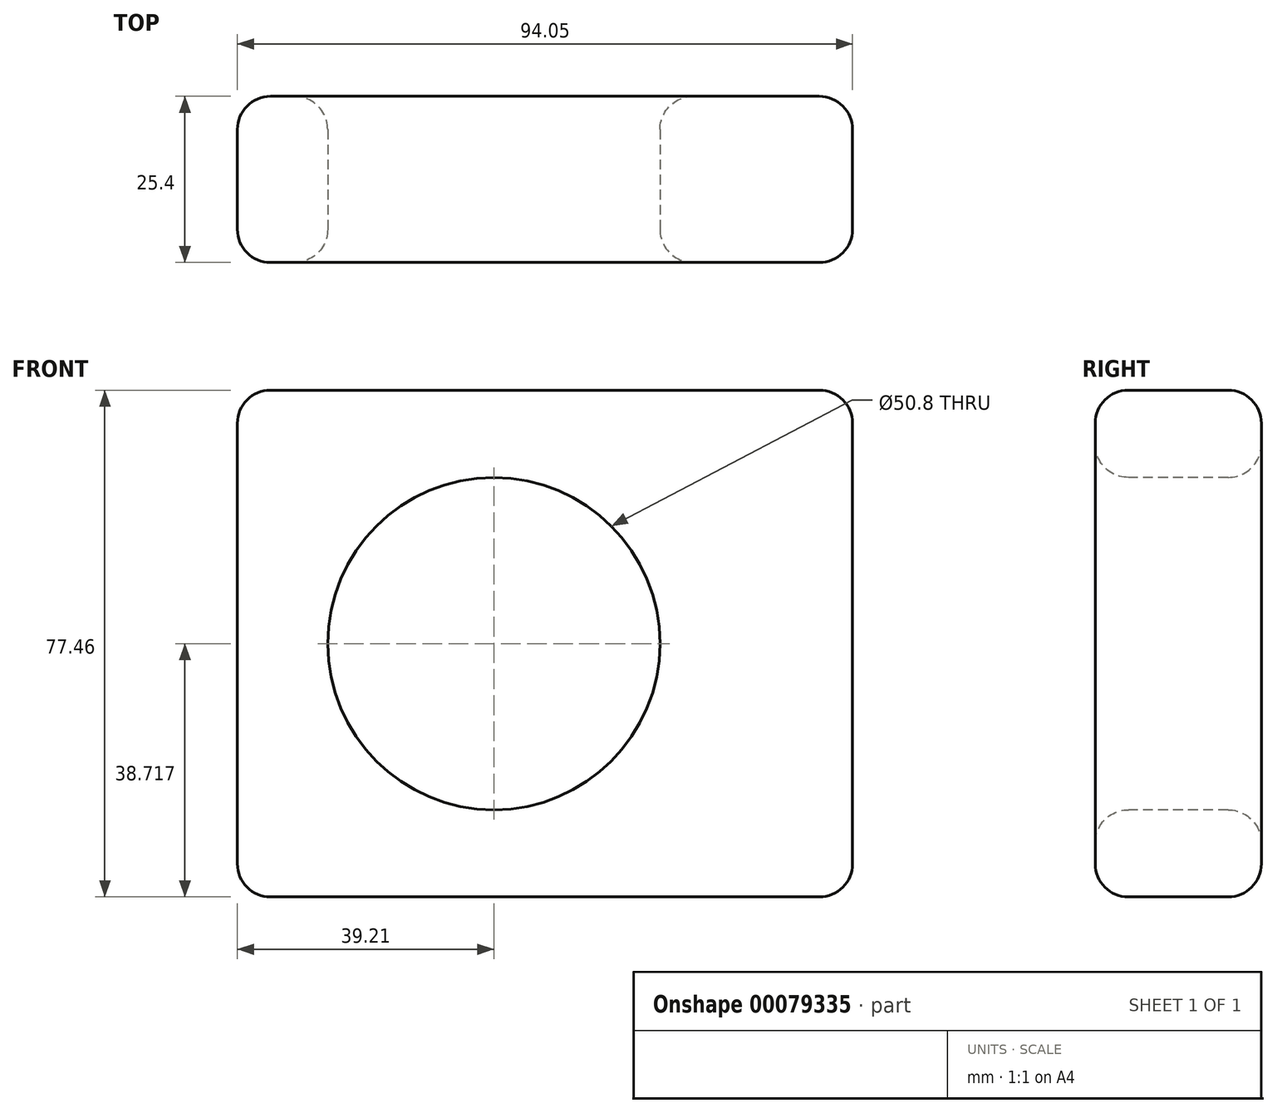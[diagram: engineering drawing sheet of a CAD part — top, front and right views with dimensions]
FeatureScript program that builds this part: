
annotation { "Feature Type Name" : "Feature", "Feature Type Description" : "" }
export const myFeature = defineFeature(function(context is Context, id is Id, definition is map)
    precondition{}
    {
        {
            var Q0;
            Q0=qCreatedBy(makeId("Front.planeOp"),FACE);
            var sketch = newSketch(context, id + "F0", { "sketchPlane" : qUnion([Q0])});
            skLineSegment(sketch, "E0.bottom", {"start": v(24.22, -20.71) * mm, "end": v(-69.83, -20.71) * mm});
            skLineSegment(sketch, "E0.top", {"start": v(24.22, 56.75) * mm, "end": v(-69.83, 56.75) * mm});
            skLineSegment(sketch, "E0.left", {"start": v(24.22, -20.71) * mm, "end": v(24.22, 56.75) * mm});
            skLineSegment(sketch, "E0.right", {"start": v(-69.83, -20.71) * mm, "end": v(-69.83, 56.75) * mm});
            skSolve(sketch);
        }
        {
            var Q0;
            Q0=makeQuery(id+"F0.imprint","IMPRINT",FACE,{"disambiguationData":[TD([[makeQuery(id+"F0.imprint","IMPRINT",EDGE,{"derivedFrom":sQuery(id+"F0.wireOp",EDGE,"E0.bottom")}),-1.0]])]});
            extrude(context, id + "F1", {"entities" : qUnion([Q0]), "depth" : 25.4 * mm});
        }
        {
            var Q0;
            Q0=makeQuery(id+"F1.opExtrude","CAP_FACE",FACE,{"disambiguationData":[OSD([sQuery(id+"F0.wireOp",EDGE,"E0.bottom"),sQuery(id+"F0.wireOp",EDGE,"E0.top"),sQuery(id+"F0.wireOp",EDGE,"E0.left"),sQuery(id+"F0.wireOp",EDGE,"E0.right")])],"isStart":false});
            var sketch = newSketch(context, id + "F2", { "sketchPlane" : qUnion([Q0])});
            skCircle(sketch, "E1", {"center": v(-30.62, 18) * mm, "radius": 8.2 * mm});
            skSolve(sketch);
        }
        {
            var Q0;
            Q0=sQuery(id+"F2.wireOp",VERTEX,"E1.center");
            var Q1;
            Q1=makeQuery(id+"F1.opExtrude","SWEPT_BODY",BODY,{"disambiguationData":[OSD([sQuery(id+"F0.wireOp",EDGE,"E0.bottom"),sQuery(id+"F0.wireOp",EDGE,"E0.top"),sQuery(id+"F0.wireOp",EDGE,"E0.left"),sQuery(id+"F0.wireOp",EDGE,"E0.right")])]});
            hole(context, id + "F3", {"style" : HoleStyle.SIMPLE, "endStyle" : HoleEndStyle.THROUGH, "holeDiameter" : 50.8 * mm, "locations" : qUnion([Q0]), "scope" : qUnion([Q1]), "isTappedThrough" : true});
        }
        {
            var Q0;
            Q0=makeQuery(id+"F1.opExtrude","CAP_FACE",FACE,{"disambiguationData":[OSD([sQuery(id+"F0.wireOp",EDGE,"E0.bottom"),sQuery(id+"F0.wireOp",EDGE,"E0.top"),sQuery(id+"F0.wireOp",EDGE,"E0.left"),sQuery(id+"F0.wireOp",EDGE,"E0.right")])],"isStart":false});
            var Q1;
            Q1=makeQuery(id+"F1.opExtrude","SWEPT_FACE",FACE,{"disambiguationData":[OSD([sQuery(id+"F0.wireOp",EDGE,"E0.top")])]});
            var Q2;
            Q2=makeQuery(id+"F1.opExtrude","SWEPT_FACE",FACE,{"disambiguationData":[OSD([sQuery(id+"F0.wireOp",EDGE,"E0.left")])]});
            var Q3;
            Q3=makeQuery(id+"F1.opExtrude","SWEPT_FACE",FACE,{"disambiguationData":[OSD([sQuery(id+"F0.wireOp",EDGE,"E0.bottom")])]});
            var Q4;
            Q4=makeQuery(id+"F1.opExtrude","CAP_FACE",FACE,{"disambiguationData":[OSD([sQuery(id+"F0.wireOp",EDGE,"E0.bottom"),sQuery(id+"F0.wireOp",EDGE,"E0.top"),sQuery(id+"F0.wireOp",EDGE,"E0.left"),sQuery(id+"F0.wireOp",EDGE,"E0.right")])],"isStart":true});
            var Q5;
            Q5=makeQuery(id+"F1.opExtrude","SWEPT_FACE",FACE,{"disambiguationData":[OSD([sQuery(id+"F0.wireOp",EDGE,"E0.right")])]});
            fillet(context, id + "F4", {"entities" : qUnion([Q0, Q1, Q2, Q3, Q4, Q5]), "radius" : 5.08 * mm, "tangentPropagation" : true, "allowEdgeOverflow" : false});
        }
    });
